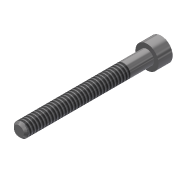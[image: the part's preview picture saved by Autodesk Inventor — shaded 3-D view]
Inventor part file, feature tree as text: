
AUTODESK INVENTOR PART (.ipt)
format: ipt  version: 2013 (Build 170138000, 138)  size: 96,768 bytes
history: native  units: in
note: dims shown in document units (in); Inventor stores cm internally (conversion verified against a paired STEP export)
features: extrude x3, sketch x3, chamfer x1, thread x1
ambient origin geometry x8: Origin, YZ Plane, XZ Plane, XY Plane, X Axis, Y Axis, Z Axis, Center Point
bodies: Solid1 (feature_tree)
feature tree (8):
  extrude  "Extrusion1"  Depth=1.25in TaperAngle=0.0deg
  extrude  "Extrusion2"  Depth=0.138in TaperAngle=0.0deg
  extrude  "Extrusion3"  Depth=0.069in TaperAngle=0.0deg
  chamfer  "Chamfer1"  Distance=0.02in Angle=45.0deg
  thread  "Thread2"  [1 undecoded]
  sketch  "Sketch1"  dims[d0=0.138in d1=1.25in d2=0.0in]
  sketch  "Sketch2"  dims[d3=0.226in d4=0.138in d5=0.0in]
  sketch  "Sketch3"  dims[d6=0.1094in d7=0.069in d8=0.0in d11=0.02in d12=0.125in d13=45.0deg d14=1.0in d15=0.0in]
note: 1 required parameter value undecoded (feature->parameter linkage not recoverable at this tier; creation-order binding heuristic only, values carry confidence <= 0.55)
